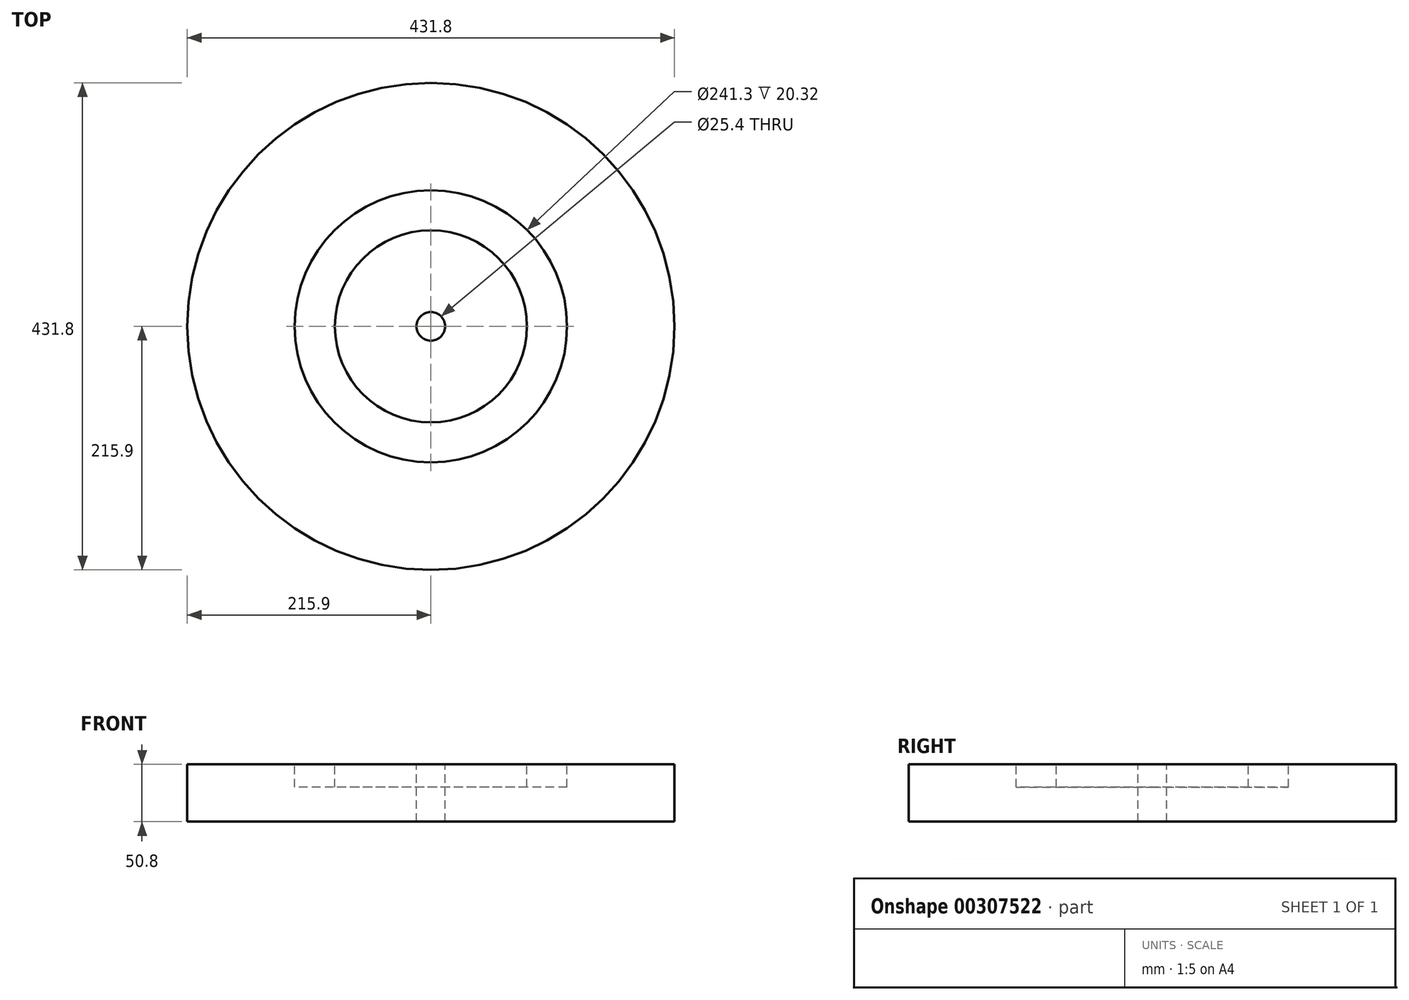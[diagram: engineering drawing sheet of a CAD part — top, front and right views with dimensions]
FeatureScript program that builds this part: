
annotation { "Feature Type Name" : "Feature", "Feature Type Description" : "" }
export const myFeature = defineFeature(function(context is Context, id is Id, definition is map)
    precondition{}
    {
        {
            var Q0;
            Q0=qCreatedBy(makeId("Top.planeOp"),FACE);
            var sketch = newSketch(context, id + "F0", { "sketchPlane" : qUnion([Q0])});
            skCircle(sketch, "E0", {"center": v(0, 0) * mm, "radius": 215.9 * mm});
            skSolve(sketch);
        }
        {
            var Q0;
            Q0 = qSketchRegion(id + "F0", true);
            extrude(context, id + "F1", {"entities" : qUnion([Q0]), "depth" : 50.8 * mm});
        }
        {
            var Q0;
            Q0=makeQuery(id+"F1.opExtrude","CAP_FACE",FACE,{"disambiguationData":[OSD([sQuery(id+"F0.wireOp",EDGE,"E0")])],"isStart":false});
            var sketch = newSketch(context, id + "F2", { "sketchPlane" : qUnion([Q0])});
            skCircle(sketch, "E1", {"center": v(0, 0) * mm, "radius": 120.65 * mm});
            skCircle(sketch, "E2", {"center": v(0, 0) * mm, "radius": 85.1 * mm});
            skSolve(sketch);
        }
        {
            var Q0;
            Q0 = qSketchRegion(id + "F2", true);
            extrude(context, id + "F3", {"entities" : qUnion([Q0]), "operationType" : NewBodyOperationType.REMOVE, "oppositeDirection" : true, "depth" : 20.32 * mm});
        }
        {
            var Q0;
            Q0=makeQuery(id+"F3.boolean.opBoolean","SPLIT",FACE,{"disambiguationData":[TD([makeQuery(id+"F3.opExtrude","SWEPT_FACE",FACE,{"disambiguationData":[OSD([sQuery(id+"F2.wireOp",EDGE,"E2")])]})])],"derivedFrom":makeQuery(id+"F1.opExtrude","CAP_FACE",FACE,{"disambiguationData":[OSD([sQuery(id+"F0.wireOp",EDGE,"E0")])],"isStart":false})});
            var sketch = newSketch(context, id + "F4", { "sketchPlane" : qUnion([Q0])});
            skCircle(sketch, "E3", {"center": v(0, 0) * mm, "radius": 12.7 * mm});
            skSolve(sketch);
        }
        {
            var Q0;
            Q0 = qSketchRegion(id + "F4", true);
            extrude(context, id + "F5", {"entities" : qUnion([Q0]), "operationType" : NewBodyOperationType.REMOVE, "endBound" : BoundingType.THROUGH_ALL, "oppositeDirection" : true, "depth" : 25.4 * mm});
        }
    });
